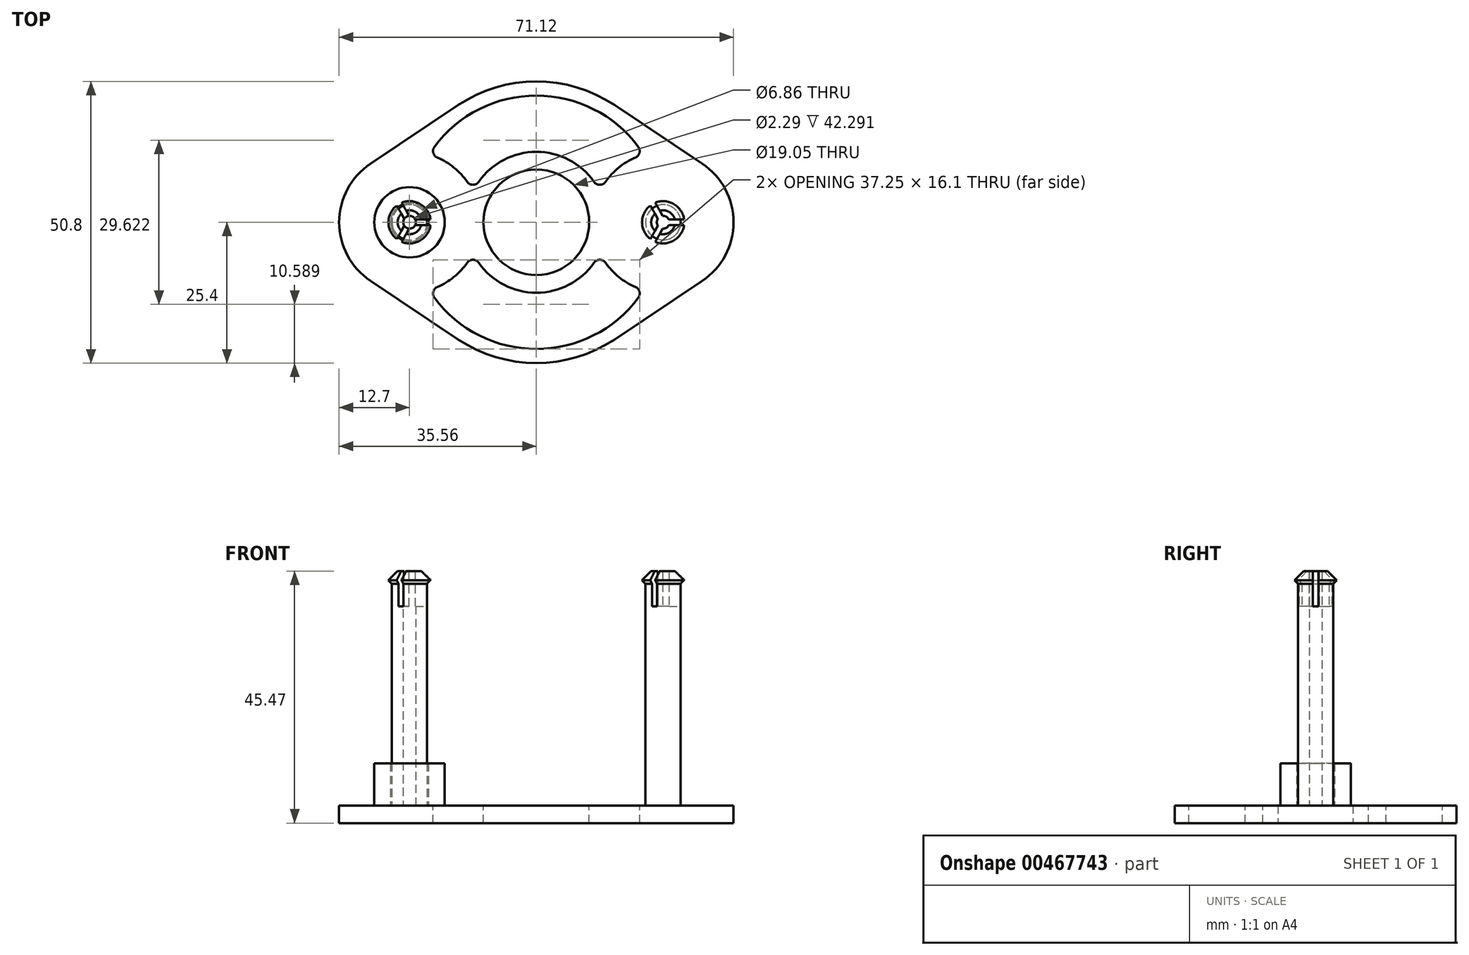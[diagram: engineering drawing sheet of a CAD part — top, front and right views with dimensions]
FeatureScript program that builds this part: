
annotation { "Feature Type Name" : "Feature", "Feature Type Description" : "" }
export const myFeature = defineFeature(function(context is Context, id is Id, definition is map)
    precondition{}
    {
        {
            var Q0;
            Q0=qCreatedBy(makeId("Front.planeOp"),FACE);
            var sketch = newSketch(context, id + "F0", { "sketchPlane" : qUnion([Q0])});
            skLineSegment(sketch, "E0", {"start": v(0, 0) * mm, "end": v(3.18, 0) * mm});
            skLineSegment(sketch, "E1", {"start": v(3.18, 0) * mm, "end": v(3.18, 40) * mm});
            skLineSegment(sketch, "E2", {"start": v(3.17, 40) * mm, "end": v(3.8, 40.64) * mm});
            skLineSegment(sketch, "E3", {"start": v(3.8, 40.64) * mm, "end": v(2.16, 42.3) * mm});
            skLineSegment(sketch, "E4", {"start": v(2.16, 42.3) * mm, "end": v(1.14, 42.3) * mm});
            skLineSegment(sketch, "E5", {"start": v(1.14, 42.3) * mm, "end": v(1.14, 0) * mm});
            skLineSegment(sketch, "E6", {"start": v(0, 0) * mm, "end": v(0, 66.19) * mm});
            skSolve(sketch);
        }
        {
            var Q0;
            {var subQ0=sQuery(id+"F0.wireOp",EDGE,"E1");Q0=makeQuery(id+"F0.imprint","IMPRINT",FACE,{"disambiguationData":[TD([[makeQuery(id+"F0.imprint","IMPRINT",EDGE,{"derivedFrom":subQ0}),1.0]])]});}
            var Q1;
            Q1=sQuery(id+"F0.wireOp",EDGE,"E6");
            revolve(context, id + "F1", {"entities" : qUnion([Q0]), "axis" : qUnion([Q1]), "revolveType" : RevolveType.FULL});
        }
        {
            var Q0;
            Q0=qCreatedBy(makeId("Top.planeOp"),FACE);
            var sketch = newSketch(context, id + "F2", { "sketchPlane" : qUnion([Q0])});
            skArc(sketch, "E7", {"start": v(-7.06, 10.56) * mm, "mid": v(-12.7, 0) * mm, "end": v(-7.06, -10.56) * mm});
            skLineSegment(sketch, "E8", {"start": v(0, 0) * mm, "end": v(45.72, 0) * mm, "construction": true});
            skArc(sketch, "E9", {"start": v(52.78, -10.56) * mm, "mid": v(58.42, 0) * mm, "end": v(52.78, 10.56) * mm});
            skArc(sketch, "E10", {"start": v(8.75, -21.12) * mm, "mid": v(22.86, -25.4) * mm, "end": v(36.97, -21.12) * mm});
            skLineSegment(sketch, "E11", {"start": v(-7.06, -10.56) * mm, "end": v(8.75, -21.12) * mm});
            skLineSegment(sketch, "E12", {"start": v(-7.06, 10.56) * mm, "end": v(8.75, 21.12) * mm});
            skLineSegment(sketch, "E13", {"start": v(36.97, 21.12) * mm, "end": v(52.78, 10.56) * mm});
            skLineSegment(sketch, "E14", {"start": v(36.97, -21.12) * mm, "end": v(52.78, -10.56) * mm});
            skArc(sketch, "E15", {"start": v(34.3, 5.54) * mm, "mid": v(22.86, 12.7) * mm, "end": v(11.43, 5.54) * mm});
            skArc(sketch, "E16.trimOffspring", {"start": v(3.53, -12.2) * mm, "mid": v(8.19, -9.7) * mm, "end": v(11.43, -5.54) * mm});
            skArc(sketch, "E17.trimOffspring", {"start": v(36.97, 21.12) * mm, "mid": v(22.86, 25.4) * mm, "end": v(8.75, 21.12) * mm});
            skArc(sketch, "E18.trimOffspring", {"start": v(42.2, 12.2) * mm, "mid": v(37.53, 9.7) * mm, "end": v(34.3, 5.54) * mm});
            skArc(sketch, "E19.trimOffspring", {"start": v(34.3, -5.54) * mm, "mid": v(37.53, -9.7) * mm, "end": v(42.2, -12.2) * mm});
            skArc(sketch, "E20.trimOffspring", {"start": v(11.43, -5.54) * mm, "mid": v(22.86, -12.7) * mm, "end": v(34.3, -5.54) * mm});
            skArc(sketch, "E21.trimOffspring", {"start": v(11.43, 5.54) * mm, "mid": v(8.19, 9.7) * mm, "end": v(3.53, 12.2) * mm});
            skArc(sketch, "E22", {"start": v(3.53, -12.2) * mm, "mid": v(22.86, -22.86) * mm, "end": v(42.2, -12.2) * mm});
            skArc(sketch, "E23.trimOffspring", {"start": v(42.2, 12.2) * mm, "mid": v(22.86, 22.86) * mm, "end": v(3.53, 12.2) * mm});
            skCircle(sketch, "E24", {"center": v(22.86, 0) * mm, "radius": 9.53 * mm});
            skSolve(sketch);
        }
        {
            var Q0;
            Q0=makeQuery(id+"F2.imprint","IMPRINT",FACE,{"disambiguationData":[TD([[makeQuery(id+"F2.imprint","IMPRINT",EDGE,{"derivedFrom":sQuery(id+"F2.wireOp",EDGE,"E7")}),1.0]])]});
            extrude(context, id + "F3", {"entities" : qUnion([Q0]), "operationType" : NewBodyOperationType.ADD, "oppositeDirection" : true, "depth" : 3.17 * mm});
        }
        {
            var Q0;
            Q0=qCreatedBy(makeId("Front.planeOp"),FACE);
            var sketch = newSketch(context, id + "F4", { "sketchPlane" : qUnion([Q0])});
            skLineSegment(sketch, "E25", {"start": v(45.72, 0) * mm, "end": v(48.9, 0) * mm});
            skLineSegment(sketch, "E26", {"start": v(48.9, 0) * mm, "end": v(48.9, 40) * mm});
            skLineSegment(sketch, "E27", {"start": v(48.9, 40) * mm, "end": v(49.53, 40.64) * mm});
            skLineSegment(sketch, "E28", {"start": v(49.53, 40.64) * mm, "end": v(47.88, 42.3) * mm});
            skLineSegment(sketch, "E29", {"start": v(47.88, 42.3) * mm, "end": v(46.86, 42.3) * mm});
            skLineSegment(sketch, "E30", {"start": v(46.86, 42.3) * mm, "end": v(46.86, 0) * mm});
            skLineSegment(sketch, "E31", {"start": v(45.72, 0) * mm, "end": v(45.72, 66.19) * mm});
            skSolve(sketch);
        }
        {
            var Q0;
            {var subQ0=sQuery(id+"F4.wireOp",EDGE,"E26");Q0=makeQuery(id+"F4.imprint","IMPRINT",FACE,{"disambiguationData":[TD([[makeQuery(id+"F4.imprint","IMPRINT",EDGE,{"derivedFrom":subQ0}),1.0]])]});}
            var Q1;
            Q1=sQuery(id+"F4.wireOp",EDGE,"E31");
            revolve(context, id + "F5", {"operationType" : NewBodyOperationType.ADD, "entities" : qUnion([Q0]), "axis" : qUnion([Q1]), "revolveType" : RevolveType.FULL});
        }
        {
            var Q0;
            Q0=makeQuery(id+"F2.imprint","IMPRINT",FACE,{"disambiguationData":[TD([[makeQuery(id+"F2.imprint","IMPRINT",EDGE,{"derivedFrom":sQuery(id+"F2.wireOp",EDGE,"E7")}),1.0]])]});
            var sketch = newSketch(context, id + "F6", { "sketchPlane" : qUnion([Q0])});
            skCircle(sketch, "E32", {"center": v(0, 0) * mm, "radius": 3.43 * mm});
            skCircle(sketch, "E33", {"center": v(0, 0) * mm, "radius": 6.35 * mm});
            skSolve(sketch);
        }
        {
            var Q0;
            Q0=makeQuery(id+"F6.imprint","IMPRINT",FACE,{"disambiguationData":[TD([[makeQuery(id+"F6.imprint","IMPRINT",EDGE,{"derivedFrom":sQuery(id+"F6.wireOp",EDGE,"E32")}),-1.0]])]});
            extrude(context, id + "F7", {"entities" : qUnion([Q0]), "depth" : 7.62 * mm});
        }
        {
            var Q0;
            Q0=makeQuery(id+"F1.opRevolve","SWEPT_FACE",FACE,{"disambiguationData":[OSD([sQuery(id+"F0.wireOp",EDGE,"E4")])]});
            var sketch = newSketch(context, id + "F8", { "sketchPlane" : qUnion([Q0])});
            skLineSegment(sketch, "E34", {"start": v(0, 0) * mm, "end": v(6.35, 0) * mm, "construction": true});
            skPoint(sketch, "E35.center", {"position": v(0, 0) * mm});
            skLineSegment(sketch, "E36.0", {"start": v(0.3, -0.5) * mm, "end": v(6.35, -0.5) * mm});
            skLineSegment(sketch, "E37", {"start": v(0, 0) * mm, "end": v(-3.17, -5.5) * mm, "construction": true});
            skLineSegment(sketch, "E38", {"start": v(0, 0) * mm, "end": v(-3.18, 5.5) * mm, "construction": true});
            skLineSegment(sketch, "E39.0", {"start": v(0.3, 0.5) * mm, "end": v(6.35, 0.5) * mm});
            skLineSegment(sketch, "E40.0", {"start": v(0.3, -0.5) * mm, "end": v(-2.74, -5.75) * mm});
            skLineSegment(sketch, "E41.0", {"start": v(-0.59, 0) * mm, "end": v(-3.61, -5.25) * mm});
            skLineSegment(sketch, "E42.0", {"start": v(0.3, 0.5) * mm, "end": v(-2.74, 5.75) * mm});
            skLineSegment(sketch, "E43.0", {"start": v(-0.59, 0) * mm, "end": v(-3.61, 5.25) * mm});
            skLineSegment(sketch, "E44", {"start": v(6.35, 0.5) * mm, "end": v(6.35, -0.5) * mm});
            skLineSegment(sketch, "E45", {"start": v(-2.74, -5.75) * mm, "end": v(-3.61, -5.25) * mm});
            skLineSegment(sketch, "E46", {"start": v(-3.61, 5.25) * mm, "end": v(-2.74, 5.75) * mm});
            skLineSegment(sketch, "E47", {"start": v(45.72, 0) * mm, "end": v(52.07, 0) * mm, "construction": true});
            skPoint(sketch, "E48.center", {"position": v(45.72, 0) * mm});
            skLineSegment(sketch, "E49.0", {"start": v(46.01, -0.5) * mm, "end": v(52.07, -0.5) * mm});
            skLineSegment(sketch, "E50", {"start": v(45.72, 0) * mm, "end": v(42.55, -5.5) * mm, "construction": true});
            skLineSegment(sketch, "E51", {"start": v(45.72, 0) * mm, "end": v(42.54, 5.5) * mm, "construction": true});
            skLineSegment(sketch, "E52.0", {"start": v(46.01, 0.5) * mm, "end": v(52.07, 0.5) * mm});
            skLineSegment(sketch, "E53.0", {"start": v(46.01, -0.5) * mm, "end": v(42.98, -5.75) * mm});
            skLineSegment(sketch, "E54.0", {"start": v(45.13, 0) * mm, "end": v(42.1, -5.25) * mm});
            skLineSegment(sketch, "E55.0", {"start": v(46.01, 0.5) * mm, "end": v(42.98, 5.75) * mm});
            skLineSegment(sketch, "E56.0", {"start": v(45.13, 0) * mm, "end": v(42.1, 5.25) * mm});
            skLineSegment(sketch, "E57", {"start": v(52.07, 0.5) * mm, "end": v(52.07, -0.5) * mm});
            skLineSegment(sketch, "E58", {"start": v(42.98, -5.75) * mm, "end": v(42.1, -5.25) * mm});
            skLineSegment(sketch, "E59", {"start": v(42.1, 5.25) * mm, "end": v(42.98, 5.75) * mm});
            skSolve(sketch);
        }
        {
            var Q0;
            {var subQ0=sQuery(id+"F8.wireOp",EDGE,"E36.0");var subQ1=sQuery(id+"F0.wireOp",EDGE,"E4");var subQ2=makeQuery(id+"F1.opRevolve","SWEPT_EDGE",EDGE,{"disambiguationData":[OSD([sQuery(id+"F0.wireOp",EDGE,"E3"),subQ1])]});var subQ3=makeQuery(id+"F8.imprint","INTERSECT",VERTEX,{"derivedFrom":[subQ2,subQ0]});Q0=makeQuery(id+"F8.imprint","IMPRINT",FACE,{"disambiguationData":[TD([[makeQuery(id+"F8.imprint","IMPRINT",EDGE,{"disambiguationData":[TD([[subQ3,1.0]])],"derivedFrom":subQ0}),1.0]])]});}
            var Q1;
            {var subQ0=sQuery(id+"F8.wireOp",EDGE,"E44");Q1=makeQuery(id+"F8.imprint","IMPRINT",FACE,{"disambiguationData":[TD([[makeQuery(id+"F8.imprint","IMPRINT",EDGE,{"derivedFrom":subQ0}),-1.0]])]});}
            var Q2;
            {var subQ0=sQuery(id+"F8.wireOp",EDGE,"E42.0");var subQ1=sQuery(id+"F0.wireOp",EDGE,"E4");var subQ2=makeQuery(id+"F1.opRevolve","SWEPT_EDGE",EDGE,{"disambiguationData":[OSD([sQuery(id+"F0.wireOp",EDGE,"E3"),subQ1])]});var subQ3=makeQuery(id+"F8.imprint","INTERSECT",VERTEX,{"derivedFrom":[subQ2,subQ0]});Q2=makeQuery(id+"F8.imprint","IMPRINT",FACE,{"disambiguationData":[TD([[makeQuery(id+"F8.imprint","IMPRINT",EDGE,{"disambiguationData":[TD([[subQ3,1.0]])],"derivedFrom":subQ0}),1.0]])]});}
            var Q3;
            {var subQ0=sQuery(id+"F8.wireOp",EDGE,"E40.0");var subQ1=sQuery(id+"F0.wireOp",EDGE,"E4");var subQ2=makeQuery(id+"F1.opRevolve","SWEPT_EDGE",EDGE,{"disambiguationData":[OSD([sQuery(id+"F0.wireOp",EDGE,"E3"),subQ1])]});var subQ3=makeQuery(id+"F8.imprint","INTERSECT",VERTEX,{"derivedFrom":[subQ2,subQ0]});Q3=makeQuery(id+"F8.imprint","IMPRINT",FACE,{"disambiguationData":[TD([[makeQuery(id+"F8.imprint","IMPRINT",EDGE,{"disambiguationData":[TD([[subQ3,1.0]])],"derivedFrom":subQ0}),-1.0]])]});}
            var Q4;
            {var subQ0=sQuery(id+"F8.wireOp",EDGE,"E45");Q4=makeQuery(id+"F8.imprint","IMPRINT",FACE,{"disambiguationData":[TD([[makeQuery(id+"F8.imprint","IMPRINT",EDGE,{"derivedFrom":subQ0}),-1.0]])]});}
            var Q5;
            {var subQ0=sQuery(id+"F8.wireOp",EDGE,"E46");Q5=makeQuery(id+"F8.imprint","IMPRINT",FACE,{"disambiguationData":[TD([[makeQuery(id+"F8.imprint","IMPRINT",EDGE,{"derivedFrom":subQ0}),-1.0]])]});}
            var Q6;
            Q6=makeQuery(id+"F8.imprint","IMPRINT",FACE,{"disambiguationData":[TD([[makeQuery(id+"F8.imprint","IMPRINT",EDGE,{"derivedFrom":sQuery(id+"F8.wireOp",EDGE,"E49.0")}),1.0]])]});
            extrude(context, id + "F9", {"entities" : qUnion([Q0, Q1, Q2, Q3, Q4, Q5, Q6]), "operationType" : NewBodyOperationType.REMOVE, "oppositeDirection" : true, "depth" : 6.35 * mm});
        }
        {
            var Q0;
            Q0=makeQuery(id+"F9.boolean.opBoolean","COPY",FACE,{"derivedFrom":makeQuery(id+"F9.opExtrude","CAP_FACE",FACE,{"disambiguationData":[OSD([sQuery(id+"F0.wireOp",EDGE,"E4"),sQuery(id+"F0.wireOp",EDGE,"E5"),sQuery(id+"F8.wireOp",EDGE,"E40.0"),sQuery(id+"F8.wireOp",EDGE,"E41.0"),sQuery(id+"F8.wireOp",EDGE,"E45")])],"isStart":false})});
            var sketch = newSketch(context, id + "F10", { "sketchPlane" : qUnion([Q0])});
            skCircle(sketch, "E60", {"center": v(0, 0) * mm, "radius": 1.27 * mm});
            skCircle(sketch, "E61", {"center": v(45.72, 0) * mm, "radius": 1.27 * mm});
            skSolve(sketch);
        }
        {
            var Q0;
            {var subQ1=sQuery(id+"F8.wireOp",EDGE,"E40.0");var subQ7=sQuery(id+"F0.wireOp",EDGE,"E5");var subQ8=sQuery(id+"F0.wireOp",EDGE,"E4");var subQ9=makeQuery(id+"F1.opRevolve","SWEPT_EDGE",EDGE,{"disambiguationData":[OSD([subQ8,subQ7])]});var subQ10=makeQuery(id+"F9.boolean.opBoolean","COPY",EDGE,{"derivedFrom":makeQuery(id+"F9.opExtrude","CAP_EDGE",EDGE,{"disambiguationData":[OSD([subQ8,subQ7]),TDD([makeQuery(id+"F8.imprint","IMPRINT",EDGE,{"disambiguationData":[TD([[makeQuery(id+"F8.imprint","INTERSECT",VERTEX,{"derivedFrom":[subQ9,subQ1]}),-1.0]])],"derivedFrom":subQ9})])],"isStart":false})});Q0=makeQuery(id+"F10.imprint","IMPRINT",FACE,{"disambiguationData":[TD([[makeQuery(id+"F10.imprint","IMPRINT",EDGE,{"derivedFrom":subQ10}),-1.0]])]});}
            var Q1;
            Q1=makeQuery(id+"F10.imprint","IMPRINT",FACE,{"disambiguationData":[TD([[makeQuery(id+"F10.imprint","IMPRINT",EDGE,{"derivedFrom":sQuery(id+"F10.wireOp",EDGE,"E61")}),1.0]])]});
            var Q2;
            Q2=makeQuery(id+"F3.opExtrude","CAP_VERTEX",VERTEX,{"disambiguationData":[OSD([sQuery(id+"F2.wireOp",EDGE,"E16.trimOffspring"),sQuery(id+"F2.wireOp",EDGE,"E20.trimOffspring")])],"isStart":false});
            extrude(context, id + "F11", {"entities" : qUnion([Q0, Q1]), "operationType" : NewBodyOperationType.ADD, "endBound" : BoundingType.UP_TO_VERTEX, "oppositeDirection" : true, "endBoundEntityVertex" : qUnion([Q2]), "depth" : 22.86 * mm, "offsetDistance" : 25.4 * mm});
        }
        {
            var Q0;
            Q0=makeQuery(id+"F3.opExtrude","SWEPT_EDGE",EDGE,{"disambiguationData":[OSD([sQuery(id+"F2.wireOp",EDGE,"E16.trimOffspring"),sQuery(id+"F2.wireOp",EDGE,"E22")])]});
            var Q1;
            Q1=makeQuery(id+"F3.opExtrude","SWEPT_EDGE",EDGE,{"disambiguationData":[OSD([sQuery(id+"F2.wireOp",EDGE,"E16.trimOffspring"),sQuery(id+"F2.wireOp",EDGE,"E20.trimOffspring")])]});
            var Q2;
            Q2=makeQuery(id+"F3.opExtrude","SWEPT_EDGE",EDGE,{"disambiguationData":[OSD([sQuery(id+"F2.wireOp",EDGE,"E19.trimOffspring"),sQuery(id+"F2.wireOp",EDGE,"E20.trimOffspring")])]});
            var Q3;
            Q3=makeQuery(id+"F3.opExtrude","SWEPT_EDGE",EDGE,{"disambiguationData":[OSD([sQuery(id+"F2.wireOp",EDGE,"E19.trimOffspring"),sQuery(id+"F2.wireOp",EDGE,"E22")])]});
            var Q4;
            Q4=makeQuery(id+"F3.opExtrude","SWEPT_EDGE",EDGE,{"disambiguationData":[OSD([sQuery(id+"F2.wireOp",EDGE,"E18.trimOffspring"),sQuery(id+"F2.wireOp",EDGE,"E23.trimOffspring")])]});
            var Q5;
            Q5=makeQuery(id+"F3.opExtrude","SWEPT_EDGE",EDGE,{"disambiguationData":[OSD([sQuery(id+"F2.wireOp",EDGE,"E15"),sQuery(id+"F2.wireOp",EDGE,"E18.trimOffspring")])]});
            var Q6;
            Q6=makeQuery(id+"F3.opExtrude","SWEPT_EDGE",EDGE,{"disambiguationData":[OSD([sQuery(id+"F2.wireOp",EDGE,"E15"),sQuery(id+"F2.wireOp",EDGE,"E21.trimOffspring")])]});
            var Q7;
            Q7=makeQuery(id+"F3.opExtrude","SWEPT_EDGE",EDGE,{"disambiguationData":[OSD([sQuery(id+"F2.wireOp",EDGE,"E21.trimOffspring"),sQuery(id+"F2.wireOp",EDGE,"E23.trimOffspring")])]});
            fillet(context, id + "F12", {"entities" : qUnion([Q0, Q1, Q2, Q3, Q4, Q5, Q6, Q7]), "radius" : 1.27 * mm, "tangentPropagation" : true, "allowEdgeOverflow" : false});
        }
    });
